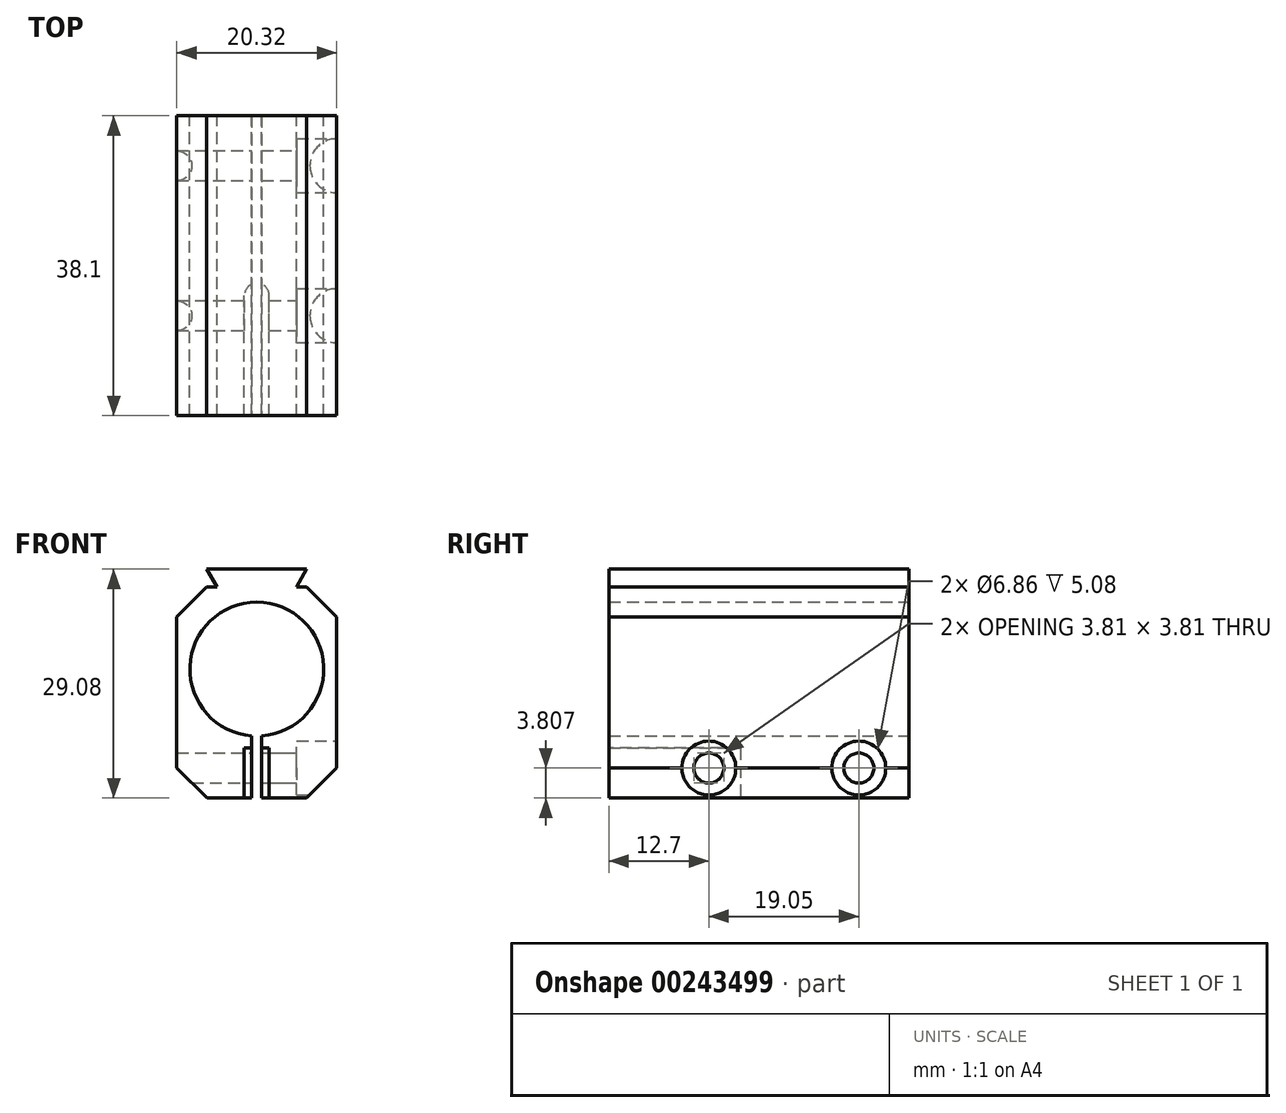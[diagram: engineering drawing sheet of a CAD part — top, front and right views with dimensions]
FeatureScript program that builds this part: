
annotation { "Feature Type Name" : "Feature", "Feature Type Description" : "" }
export const myFeature = defineFeature(function(context is Context, id is Id, definition is map)
    precondition{}
    {
        {
            var Q0;
            Q0=qCreatedBy(makeId("Front.planeOp"),FACE);
            var sketch = newSketch(context, id + "F0", { "sketchPlane" : qUnion([Q0])});
            skCircle(sketch, "E0", {"center": v(0, 0) * mm, "radius": 8.5 * mm});
            skLineSegment(sketch, "E1.bottom", {"start": v(-6.35, 12.7) * mm, "end": v(6.35, 12.7) * mm});
            skLineSegment(sketch, "E1.top", {"start": v(-6.35, -16.38) * mm, "end": v(6.35, -16.38) * mm});
            skLineSegment(sketch, "E1.left", {"start": v(-10.16, 6.6) * mm, "end": v(-10.16, -12.57) * mm});
            skLineSegment(sketch, "E1.right", {"start": v(10.16, 6.6) * mm, "end": v(10.16, -12.57) * mm});
            skLineSegment(sketch, "E2.bottom", {"start": v(-5.03, 10.41) * mm, "end": v(5.03, 10.41) * mm});
            skPoint(sketch, "E2.middle", {"position": v(0, 12.7) * mm});
            skLineSegment(sketch, "E3", {"start": v(-6.35, 12.7) * mm, "end": v(-5.03, 10.41) * mm});
            skLineSegment(sketch, "E4", {"start": v(6.35, 12.7) * mm, "end": v(5.03, 10.41) * mm});
            skLineSegment(sketch, "E5", {"start": v(-6.35, 10.41) * mm, "end": v(6.35, 10.41) * mm});
            skLineSegment(sketch, "E6", {"start": v(-6.35, 10.41) * mm, "end": v(-10.16, 6.6) * mm});
            skLineSegment(sketch, "E7", {"start": v(6.35, 10.41) * mm, "end": v(10.16, 6.6) * mm});
            skPoint(sketch, "E8.orphan", {"position": v(10.16, 12.7) * mm});
            skPoint(sketch, "E9.orphan", {"position": v(-10.16, 10.41) * mm});
            skPoint(sketch, "E10.orphan", {"position": v(-10.16, 12.7) * mm});
            skLineSegment(sketch, "E11", {"start": v(-6.35, -16.38) * mm, "end": v(-10.16, -12.57) * mm});
            skLineSegment(sketch, "E12", {"start": v(6.35, -16.38) * mm, "end": v(10.16, -12.57) * mm});
            skPoint(sketch, "E13.orphan", {"position": v(10.16, -16.38) * mm});
            skPoint(sketch, "E14.orphan", {"position": v(-10.16, -16.38) * mm});
            skSolve(sketch);
        }
        {
            var Q0;
            Q0=makeQuery(id+"F0.imprint","IMPRINT",FACE,{"disambiguationData":[TD([[makeQuery(id+"F0.imprint","IMPRINT",EDGE,{"derivedFrom":sQuery(id+"F0.wireOp",EDGE,"E0")}),-1.0]])]});
            var Q1;
            {var subQ0=sQuery(id+"F0.wireOp",EDGE,"E3");Q1=makeQuery(id+"F0.imprint","IMPRINT",FACE,{"disambiguationData":[TD([[makeQuery(id+"F0.imprint","IMPRINT",EDGE,{"derivedFrom":subQ0}),1.0]])]});}
            var Q2;
            {var subQ3=sQuery(id+"F0.wireOp",EDGE,"QEQgPhsT-h42j-z6O1-aMj6-YpYyurqOfbAo");Q2=makeQuery(id+"F0.imprint","IMPRINT",FACE,{"disambiguationData":[TD([[makeQuery(id+"F0.imprint","IMPRINT",EDGE,{"derivedFrom":subQ3}),-1.0]])]});}
            var Q3;
            {var subQ3=sQuery(id+"F0.wireOp",EDGE,"83csRBov-P8IX-huAB-eNqn-EXorecRITSEa");Q3=makeQuery(id+"F0.imprint","IMPRINT",FACE,{"disambiguationData":[TD([[makeQuery(id+"F0.imprint","IMPRINT",EDGE,{"derivedFrom":subQ3}),1.0]])]});}
            extrude(context, id + "F1", {"entities" : qUnion([Q0, Q1, Q2, Q3]), "depth" : 38.1 * mm});
        }
        {
            var Q0;
            Q0=makeQuery(id+"F1.opExtrude","SWEPT_FACE",FACE,{"disambiguationData":[OSD([sQuery(id+"F0.wireOp",EDGE,"E1.top")])]});
            var sketch = newSketch(context, id + "F2", { "sketchPlane" : qUnion([Q0])});
            skLineSegment(sketch, "E15.bottom", {"start": v(-1.59, 38.1) * mm, "end": v(1.59, 38.1) * mm});
            skLineSegment(sketch, "E15.left", {"start": v(-1.59, 38.1) * mm, "end": v(-1.59, 22.86) * mm});
            skLineSegment(sketch, "E15.right", {"start": v(1.59, 38.1) * mm, "end": v(1.59, 22.86) * mm});
            skPoint(sketch, "E15.middle", {"position": v(0, 30.48) * mm});
            skArc(sketch, "E16", {"start": v(-1.59, 22.86) * mm, "mid": v(0, 21.27) * mm, "end": v(1.59, 22.86) * mm});
            skSolve(sketch);
        }
        {
            var Q0;
            Q0=makeQuery(id+"F2.imprint","IMPRINT",FACE,{"disambiguationData":[TD([[makeQuery(id+"F2.imprint","IMPRINT",EDGE,{"derivedFrom":sQuery(id+"F2.wireOp",EDGE,"E15.bottom")}),-1.0]])]});
            extrude(context, id + "F3", {"entities" : qUnion([Q0]), "operationType" : NewBodyOperationType.REMOVE, "oppositeDirection" : true, "depth" : 6.35 * mm});
        }
        {
            var Q0;
            Q0=makeQuery(id+"F1.opExtrude","SWEPT_FACE",FACE,{"disambiguationData":[OSD([sQuery(id+"F0.wireOp",EDGE,"E1.right")])]});
            var sketch = newSketch(context, id + "F4", { "sketchPlane" : qUnion([Q0])});
            skCircle(sketch, "E17", {"center": v(-25.4, -12.57) * mm, "radius": 3.43 * mm});
            skCircle(sketch, "E18", {"center": v(-6.35, -12.57) * mm, "radius": 3.43 * mm});
            skPoint(sketch, "E19.start.orphan", {"position": v(-38.1, -12.57) * mm});
            skPoint(sketch, "E20.orphan", {"position": v(0, -12.57) * mm});
            skCircle(sketch, "E21", {"center": v(-25.4, -12.57) * mm, "radius": 1.9 * mm});
            skCircle(sketch, "E22", {"center": v(-6.35, -12.57) * mm, "radius": 1.9 * mm});
            skSolve(sketch);
        }
        {
            var Q0;
            {var subQ0=sQuery(id+"F4.wireOp",EDGE,"E17");var subQ1=makeQuery(id+"F1.opExtrude","SWEPT_EDGE",EDGE,{"disambiguationData":[OSD([sQuery(id+"F0.wireOp",EDGE,"E1.right"),sQuery(id+"F0.wireOp",EDGE,"E12")])]});var subQ2=makeQuery(id+"F4.imprint","INTERSECT",VERTEX,{"disambiguationData":[OD(0.0)],"derivedFrom":[subQ1,subQ0]});Q0=makeQuery(id+"F4.imprint","IMPRINT",FACE,{"disambiguationData":[TD([[makeQuery(id+"F4.imprint","IMPRINT",EDGE,{"disambiguationData":[TD([[subQ2,-1.0]])],"derivedFrom":subQ0}),1.0]])]});}
            var Q1;
            {var subQ0=sQuery(id+"F4.wireOp",EDGE,"E18");var subQ1=makeQuery(id+"F1.opExtrude","SWEPT_EDGE",EDGE,{"disambiguationData":[OSD([sQuery(id+"F0.wireOp",EDGE,"E1.right"),sQuery(id+"F0.wireOp",EDGE,"E12")])]});var subQ2=makeQuery(id+"F4.imprint","INTERSECT",VERTEX,{"disambiguationData":[OD(0.0)],"derivedFrom":[subQ1,subQ0]});Q1=makeQuery(id+"F4.imprint","IMPRINT",FACE,{"disambiguationData":[TD([[makeQuery(id+"F4.imprint","IMPRINT",EDGE,{"disambiguationData":[TD([[subQ2,1.0]])],"derivedFrom":subQ0}),1.0]])]});}
            var Q2;
            {var subQ0=sQuery(id+"F4.wireOp",EDGE,"E18");var subQ1=makeQuery(id+"F1.opExtrude","SWEPT_EDGE",EDGE,{"disambiguationData":[OSD([sQuery(id+"F0.wireOp",EDGE,"E1.right"),sQuery(id+"F0.wireOp",EDGE,"E12")])]});var subQ2=makeQuery(id+"F4.imprint","INTERSECT",VERTEX,{"disambiguationData":[OD(0.0)],"derivedFrom":[subQ1,subQ0]});Q2=makeQuery(id+"F4.imprint","IMPRINT",FACE,{"disambiguationData":[TD([[makeQuery(id+"F4.imprint","IMPRINT",EDGE,{"disambiguationData":[TD([[subQ2,-1.0]])],"derivedFrom":subQ0}),1.0]])]});}
            var Q3;
            {var subQ0=sQuery(id+"F4.wireOp",EDGE,"E17");var subQ1=makeQuery(id+"F1.opExtrude","SWEPT_EDGE",EDGE,{"disambiguationData":[OSD([sQuery(id+"F0.wireOp",EDGE,"E1.right"),sQuery(id+"F0.wireOp",EDGE,"E12")])]});var subQ2=makeQuery(id+"F4.imprint","INTERSECT",VERTEX,{"disambiguationData":[OD(0.0)],"derivedFrom":[subQ1,subQ0]});Q3=makeQuery(id+"F4.imprint","IMPRINT",FACE,{"disambiguationData":[TD([[makeQuery(id+"F4.imprint","IMPRINT",EDGE,{"disambiguationData":[TD([[subQ2,1.0]])],"derivedFrom":subQ0}),1.0]])]});}
            extrude(context, id + "F5", {"entities" : qUnion([Q0, Q1, Q2, Q3]), "operationType" : NewBodyOperationType.REMOVE, "oppositeDirection" : true, "depth" : 5.08 * mm});
        }
        {
            var Q0;
            Q0=makeQuery(id+"F5.boolean.opBoolean","SPLIT",FACE,{"disambiguationData":[TD([makeQuery(id+"F5.opExtrude","SWEPT_FACE",FACE,{"disambiguationData":[OSD([sQuery(id+"F4.wireOp",EDGE,"E21")])]})])],"derivedFrom":makeQuery(id+"F1.opExtrude","SWEPT_FACE",FACE,{"disambiguationData":[OSD([sQuery(id+"F0.wireOp",EDGE,"E1.right")])]})});
            var Q1;
            Q1=makeQuery(id+"F5.boolean.opBoolean","SPLIT",FACE,{"disambiguationData":[TD([makeQuery(id+"F5.opExtrude","SWEPT_FACE",FACE,{"disambiguationData":[OSD([sQuery(id+"F4.wireOp",EDGE,"E21")])]})])],"derivedFrom":makeQuery(id+"F1.opExtrude","SWEPT_FACE",FACE,{"disambiguationData":[OSD([sQuery(id+"F0.wireOp",EDGE,"E12")])]})});
            var Q2;
            Q2=makeQuery(id+"F5.boolean.opBoolean","SPLIT",FACE,{"disambiguationData":[TD([makeQuery(id+"F5.opExtrude","SWEPT_FACE",FACE,{"disambiguationData":[OSD([sQuery(id+"F4.wireOp",EDGE,"E22")])]})])],"derivedFrom":makeQuery(id+"F1.opExtrude","SWEPT_FACE",FACE,{"disambiguationData":[OSD([sQuery(id+"F0.wireOp",EDGE,"E1.right")])]})});
            var Q3;
            Q3=makeQuery(id+"F5.boolean.opBoolean","SPLIT",FACE,{"disambiguationData":[TD([makeQuery(id+"F5.opExtrude","SWEPT_FACE",FACE,{"disambiguationData":[OSD([sQuery(id+"F4.wireOp",EDGE,"E22")])]})])],"derivedFrom":makeQuery(id+"F1.opExtrude","SWEPT_FACE",FACE,{"disambiguationData":[OSD([sQuery(id+"F0.wireOp",EDGE,"E12")])]})});
            extrude(context, id + "F6", {"entities" : qUnion([Q0, Q1, Q2, Q3]), "operationType" : NewBodyOperationType.REMOVE, "endBound" : BoundingType.THROUGH_ALL, "oppositeDirection" : true, "depth" : 25.4 * mm});
        }
        {
            var Q0;
            Q0=makeQuery(id+"F1.opExtrude","SWEPT_FACE",FACE,{"disambiguationData":[OSD([sQuery(id+"F0.wireOp",EDGE,"E1.top")])]});
            var sketch = newSketch(context, id + "F7", { "sketchPlane" : qUnion([Q0])});
            skLineSegment(sketch, "E23.bottom", {"start": v(0.63, 0) * mm, "end": v(-0.64, 0) * mm});
            skLineSegment(sketch, "E23.top", {"start": v(0.63, 38.1) * mm, "end": v(-0.64, 38.1) * mm});
            skLineSegment(sketch, "E23.left", {"start": v(0.63, 0) * mm, "end": v(0.63, 38.1) * mm});
            skLineSegment(sketch, "E23.right", {"start": v(-0.64, 0) * mm, "end": v(-0.64, 38.1) * mm});
            skPoint(sketch, "E23.middle", {"position": v(0, 19.05) * mm});
            skSolve(sketch);
        }
        {
            var Q0;
            {var subQ0=sQuery(id+"F7.wireOp",EDGE,"E23.bottom");Q0=makeQuery(id+"F7.imprint","IMPRINT",FACE,{"disambiguationData":[TD([[makeQuery(id+"F7.imprint","IMPRINT",EDGE,{"derivedFrom":subQ0}),1.0]])]});}
            var Q1;
            {var subQ0=sQuery(id+"F7.wireOp",EDGE,"E23.top");Q1=makeQuery(id+"F7.imprint","IMPRINT",FACE,{"disambiguationData":[TD([[makeQuery(id+"F7.imprint","IMPRINT",EDGE,{"derivedFrom":subQ0}),1.0]])]});}
            var Q2;
            Q2=makeQuery(id+"F1.opExtrude","SWEPT_FACE",FACE,{"disambiguationData":[OSD([sQuery(id+"F0.wireOp",EDGE,"E0")])]});
            extrude(context, id + "F8", {"entities" : qUnion([Q0, Q1]), "operationType" : NewBodyOperationType.REMOVE, "endBound" : BoundingType.UP_TO_SURFACE, "oppositeDirection" : true, "endBoundEntityFace" : qUnion([Q2]), "depth" : 25.4 * mm});
        }
    });
